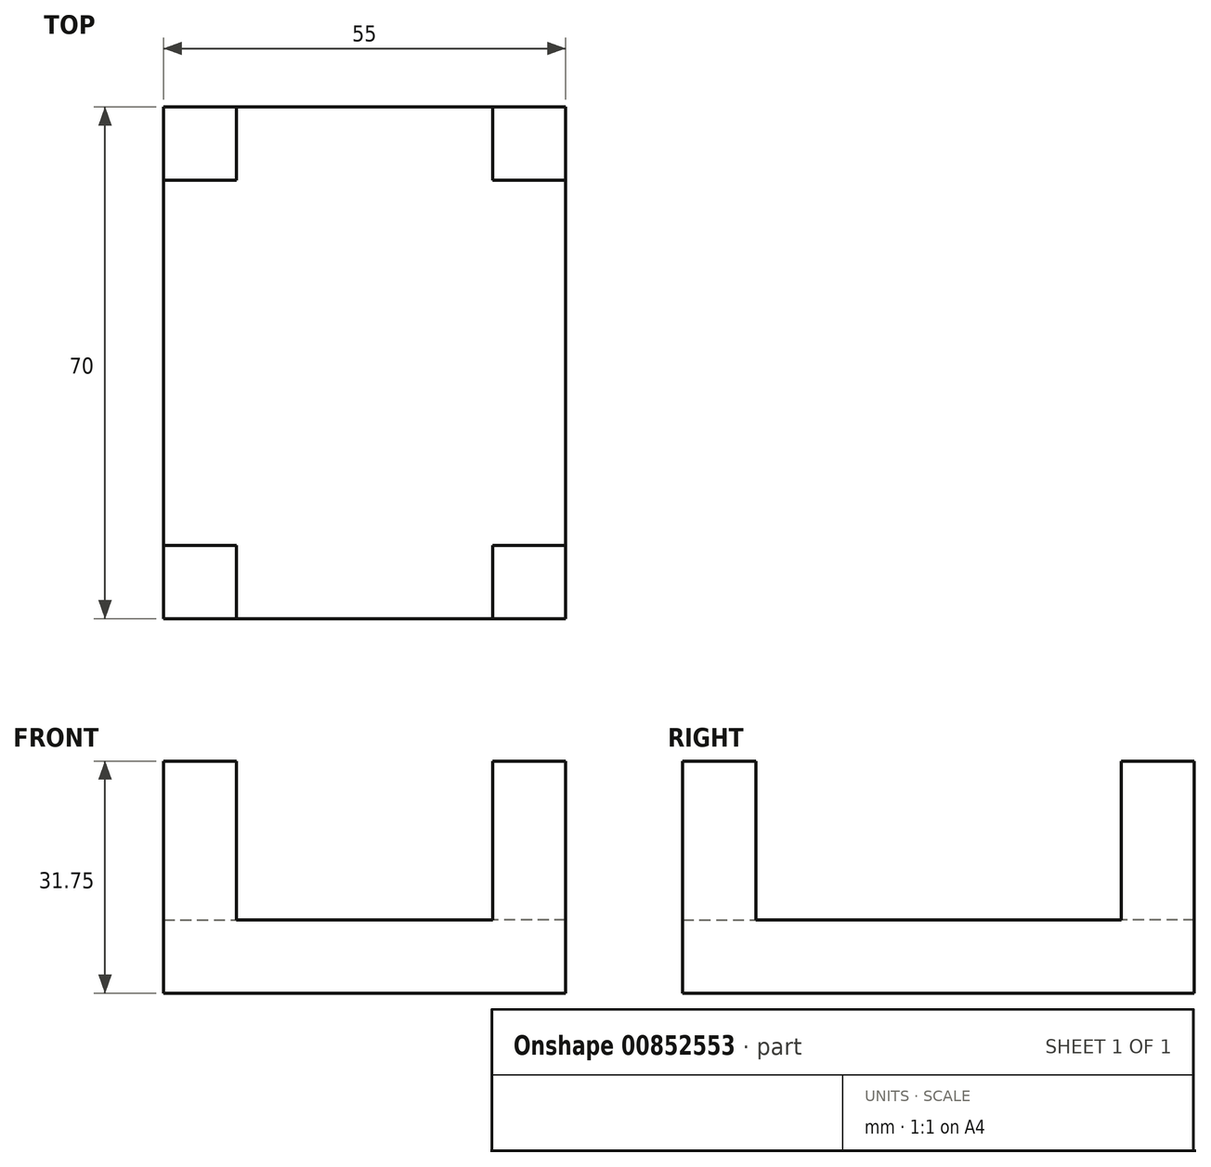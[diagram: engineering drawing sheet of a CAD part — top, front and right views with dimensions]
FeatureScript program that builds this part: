
annotation { "Feature Type Name" : "Feature", "Feature Type Description" : "" }
export const myFeature = defineFeature(function(context is Context, id is Id, definition is map)
    precondition{}
    {
        {
            var Q0;
            Q0=qCreatedBy(makeId("Top.planeOp"),FACE);
            var sketch = newSketch(context, id + "F0", { "sketchPlane" : qUnion([Q0])});
            skLineSegment(sketch, "E0.bottom", {"start": v(27.5, -35) * mm, "end": v(-27.5, -35) * mm});
            skLineSegment(sketch, "E0.top", {"start": v(27.5, 35) * mm, "end": v(-27.5, 35) * mm});
            skLineSegment(sketch, "E0.left", {"start": v(27.5, -35) * mm, "end": v(27.5, 35) * mm});
            skLineSegment(sketch, "E0.right", {"start": v(-27.5, -35) * mm, "end": v(-27.5, 35) * mm});
            skPoint(sketch, "E0.middle", {"position": v(0, 0) * mm});
            skLineSegment(sketch, "E1.bottom", {"start": v(-27.5, -35) * mm, "end": v(-17.5, -35) * mm});
            skLineSegment(sketch, "E1.top", {"start": v(-27.5, -25) * mm, "end": v(-17.5, -25) * mm});
            skLineSegment(sketch, "E1.left", {"start": v(-27.5, -35) * mm, "end": v(-27.5, -25) * mm});
            skLineSegment(sketch, "E1.right", {"start": v(-17.5, -35) * mm, "end": v(-17.5, -25) * mm});
            skLineSegment(sketch, "E2", {"start": v(0, 35) * mm, "end": v(0, -35) * mm});
            skLineSegment(sketch, "E3.MirrorCS", {"start": v(27.5, -25) * mm, "end": v(17.5, -25) * mm});
            skLineSegment(sketch, "E4.MirrorCS", {"start": v(17.5, -35) * mm, "end": v(17.5, -25) * mm});
            skLineSegment(sketch, "E5.MirrorCS", {"start": v(27.5, -35) * mm, "end": v(17.5, -35) * mm});
            skLineSegment(sketch, "E6.MirrorCS", {"start": v(27.5, -35) * mm, "end": v(27.5, -25) * mm});
            skLineSegment(sketch, "E7", {"start": v(-27.5, 0) * mm, "end": v(27.5, 0) * mm});
            skLineSegment(sketch, "E8.MirrorCS", {"start": v(-27.5, 25) * mm, "end": v(-17.5, 25) * mm});
            skLineSegment(sketch, "E9.MirrorCS", {"start": v(-17.5, 35) * mm, "end": v(-17.5, 25) * mm});
            skLineSegment(sketch, "E10.MirrorCS", {"start": v(17.5, 35) * mm, "end": v(17.5, 25) * mm});
            skLineSegment(sketch, "E11.MirrorCS", {"start": v(27.5, 25) * mm, "end": v(17.5, 25) * mm});
            skLineSegment(sketch, "E12.MirrorCS", {"start": v(27.5, 35) * mm, "end": v(17.5, 35) * mm});
            skLineSegment(sketch, "E13.MirrorCS", {"start": v(-27.5, 35) * mm, "end": v(-17.5, 35) * mm});
            skLineSegment(sketch, "E14.MirrorCS", {"start": v(-27.5, 35) * mm, "end": v(-27.5, 25) * mm});
            skLineSegment(sketch, "E15.MirrorCS", {"start": v(27.5, 35) * mm, "end": v(27.5, 25) * mm});
            skSolve(sketch);
        }
        {
            var Q0;
            {var subQ1=sQuery(id+"F0.wireOp",EDGE,"E1.top");Q0=makeQuery(id+"F0.imprint","IMPRINT",FACE,{"disambiguationData":[TD([[makeQuery(id+"F0.imprint","IMPRINT",EDGE,{"derivedFrom":subQ1}),1.0]])]});}
            var Q1;
            {var subQ7=sQuery(id+"F0.wireOp",EDGE,"E8.MirrorCS");Q1=makeQuery(id+"F0.imprint","IMPRINT",FACE,{"disambiguationData":[TD([[makeQuery(id+"F0.imprint","IMPRINT",EDGE,{"derivedFrom":subQ7}),-1.0]])]});}
            var Q2;
            {var subQ8=sQuery(id+"F0.wireOp",EDGE,"E10.MirrorCS");Q2=makeQuery(id+"F0.imprint","IMPRINT",FACE,{"disambiguationData":[TD([[makeQuery(id+"F0.imprint","IMPRINT",EDGE,{"derivedFrom":subQ8}),-1.0]])]});}
            var Q3;
            {var subQ7=sQuery(id+"F0.wireOp",EDGE,"E3.MirrorCS");Q3=makeQuery(id+"F0.imprint","IMPRINT",FACE,{"disambiguationData":[TD([[makeQuery(id+"F0.imprint","IMPRINT",EDGE,{"derivedFrom":subQ7}),-1.0]])]});}
            extrude(context, id + "F1", {"entities" : qUnion([Q0, Q1, Q2, Q3]), "depth" : 10 * mm, "offsetDistance" : 25 * mm});
        }
        {
            var Q0;
            {var subQ0=sQuery(id+"F0.wireOp",EDGE,"E10.MirrorCS");Q0=makeQuery(id+"F0.imprint","IMPRINT",FACE,{"disambiguationData":[TD([[makeQuery(id+"F0.imprint","IMPRINT",EDGE,{"derivedFrom":subQ0}),1.0]])]});}
            var Q1;
            {var subQ4=sQuery(id+"F0.wireOp",EDGE,"E8.MirrorCS");Q1=makeQuery(id+"F0.imprint","IMPRINT",FACE,{"disambiguationData":[TD([[makeQuery(id+"F0.imprint","IMPRINT",EDGE,{"derivedFrom":subQ4}),1.0]])]});}
            var Q2;
            {var subQ4=sQuery(id+"F0.wireOp",EDGE,"E1.top");Q2=makeQuery(id+"F0.imprint","IMPRINT",FACE,{"disambiguationData":[TD([[makeQuery(id+"F0.imprint","IMPRINT",EDGE,{"derivedFrom":subQ4}),-1.0]])]});}
            var Q3;
            {var subQ4=sQuery(id+"F0.wireOp",EDGE,"E3.MirrorCS");Q3=makeQuery(id+"F0.imprint","IMPRINT",FACE,{"disambiguationData":[TD([[makeQuery(id+"F0.imprint","IMPRINT",EDGE,{"derivedFrom":subQ4}),1.0]])]});}
            extrude(context, id + "F2", {"entities" : qUnion([Q0, Q1, Q2, Q3]), "operationType" : NewBodyOperationType.ADD, "depth" : 31.75 * mm, "offsetDistance" : 25 * mm});
        }
    });
